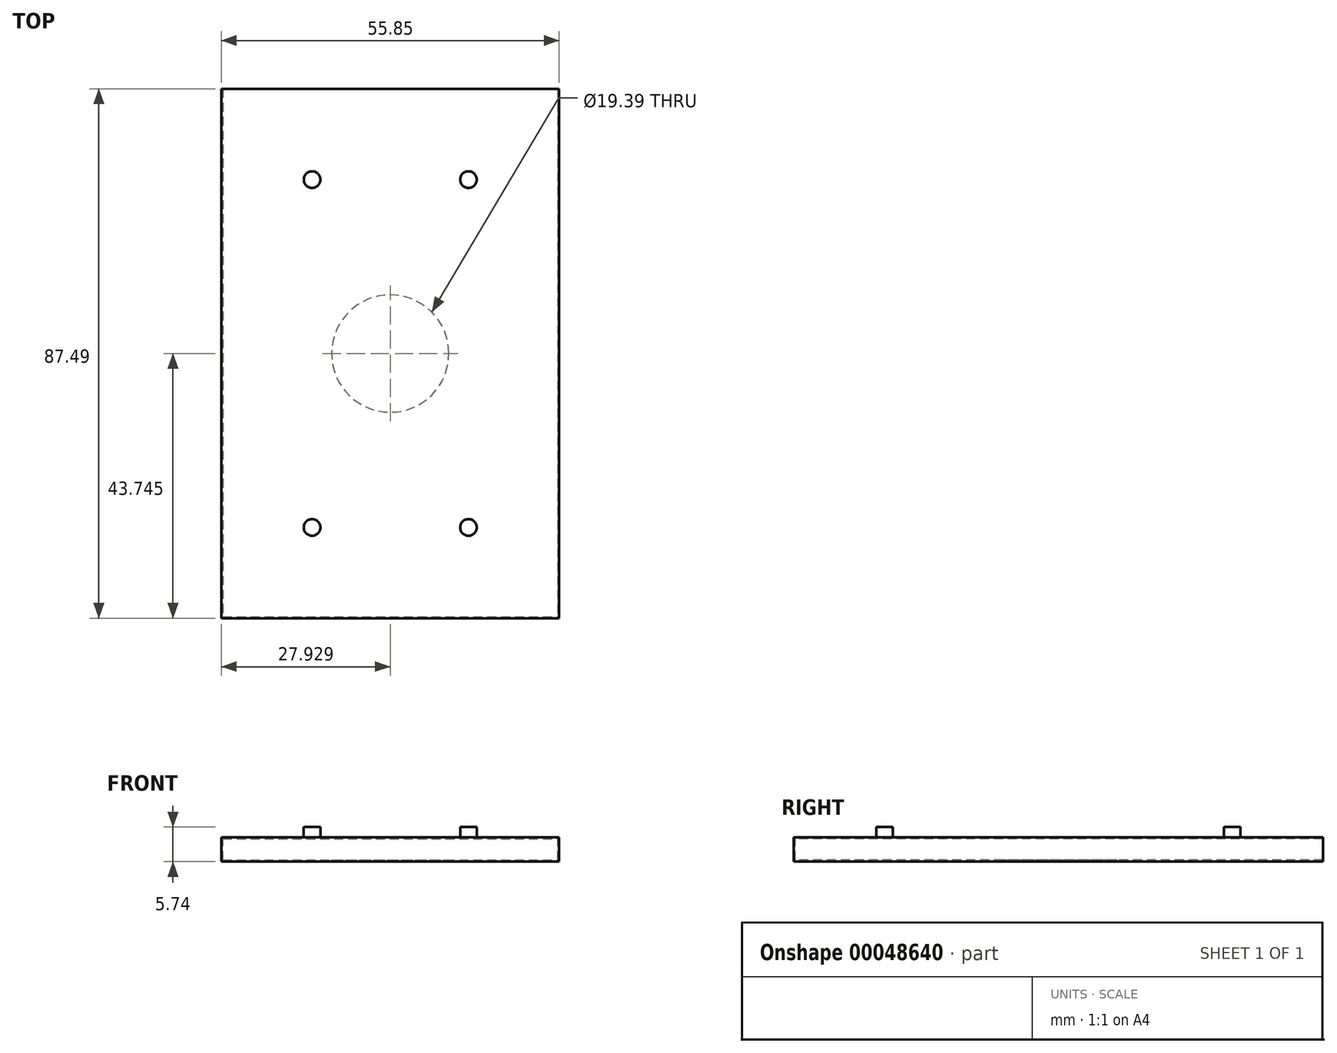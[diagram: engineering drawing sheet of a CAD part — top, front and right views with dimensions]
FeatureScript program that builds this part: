
annotation { "Feature Type Name" : "Feature", "Feature Type Description" : "" }
export const myFeature = defineFeature(function(context is Context, id is Id, definition is map)
    precondition{}
    {
        {
            var Q0;
            Q0=qCreatedBy(makeId("Front.planeOp"),FACE);
            var sketch = newSketch(context, id + "F0", { "sketchPlane" : qUnion([Q0])});
            skLineSegment(sketch, "E0.bottom", {"start": v(-66.96, -20.03) * mm, "end": v(-11.1, -20.03) * mm});
            skLineSegment(sketch, "E0.top", {"start": v(-66.96, -23.03) * mm, "end": v(-11.1, -23.03) * mm});
            skLineSegment(sketch, "E0.left", {"start": v(-66.96, -20.03) * mm, "end": v(-66.96, -23.03) * mm});
            skLineSegment(sketch, "E0.right", {"start": v(-11.1, -20.03) * mm, "end": v(-11.1, -23.03) * mm});
            skSolve(sketch);
        }
        {
            var Q0;
            Q0=makeQuery(id+"F0.imprint","IMPRINT",FACE,{"disambiguationData":[TD([[makeQuery(id+"F0.imprint","IMPRINT",EDGE,{"derivedFrom":sQuery(id+"F0.wireOp",EDGE,"E0.bottom")}),-1.0]])]});
            extrude(context, id + "F1", {"entities" : qUnion([Q0]), "oppositeDirection" : true, "depth" : 87.49 * mm});
        }
        {
            var Q0;
            Q0=makeQuery(id+"F1.opExtrude","SWEPT_FACE",FACE,{"disambiguationData":[OSD([sQuery(id+"F0.wireOp",EDGE,"E0.bottom")])]});
            shell(context, id + "F2", {"entities" : qUnion([Q0]), "thickness" : 0.75 * mm});
        }
        {
            var Q0;
            {var subQ0=sQuery(id+"F0.wireOp",EDGE,"E0.bottom");var subQ1=sQuery(id+"F0.wireOp",EDGE,"E0.top");var subQ2=sQuery(id+"F0.wireOp",EDGE,"E0.left");var subQ3=sQuery(id+"F0.wireOp",EDGE,"E0.right");Q0=makeQuery(id+"F2.opShell","OFFSET_FACE",FACE,{"disambiguationData":[OSD([subQ0,subQ1,subQ2,subQ3]),TDD([makeQuery(id+"F1.opExtrude","CAP_FACE",FACE,{"disambiguationData":[OSD([subQ0,subQ1,subQ2,subQ3])],"isStart":false})])]});}
            extrude(context, id + "F3", {"entities" : qUnion([Q0]), "operationType" : NewBodyOperationType.REMOVE, "oppositeDirection" : true, "depth" : 0.75 * mm});
        }
        {
            var Q0;
            {var subQ0=sQuery(id+"F0.wireOp",EDGE,"E0.top");Q0=makeQuery(id+"F3.boolean.opBoolean","MERGE",FACE,{"derivedFrom":[makeQuery(id+"F2.opShell","OFFSET_FACE",FACE,{"disambiguationData":[OSD([subQ0])]}),makeQuery(id+"F3.opExtrude","SWEPT_FACE",FACE,{"disambiguationData":[OSD([subQ0])]})]});}
            var sketch = newSketch(context, id + "F4", { "sketchPlane" : qUnion([Q0])});
            skPoint(sketch, "E1", {"position": v(-39.03, 87.49) * mm});
            skPoint(sketch, "E2", {"position": v(-49.03, 87.49) * mm});
            skPoint(sketch, "E3", {"position": v(-29.03, 87.49) * mm});
            skLineSegment(sketch, "E4", {"start": v(-49.03, 87.49) * mm, "end": v(-49.03, 94.5) * mm});
            skLineSegment(sketch, "E5", {"start": v(-49.03, 94.5) * mm, "end": v(-29.03, 94.5) * mm});
            skLineSegment(sketch, "E6", {"start": v(-29.03, 94.5) * mm, "end": v(-29.03, 87.49) * mm});
            skPoint(sketch, "E7.end.orphan", {"position": v(-43.53, 87.49) * mm});
            skPoint(sketch, "E7.start.orphan", {"position": v(-34.53, 87.49) * mm});
            skLineSegment(sketch, "E8.bottom", {"start": v(-47.03, 89.5) * mm, "end": v(-31.03, 89.5) * mm});
            skLineSegment(sketch, "E8.top", {"start": v(-47.03, 92.5) * mm, "end": v(-31.03, 92.5) * mm});
            skLineSegment(sketch, "E8.left", {"start": v(-47.03, 89.5) * mm, "end": v(-47.03, 92.5) * mm});
            skLineSegment(sketch, "E8.right", {"start": v(-31.03, 89.5) * mm, "end": v(-31.03, 92.5) * mm});
            skSolve(sketch);
        }
        {
            var Q0;
            {var subQ2=sQuery(id+"F4.wireOp",EDGE,"E4");Q0=makeQuery(id+"F4.imprint","IMPRINT",FACE,{"disambiguationData":[TD([[makeQuery(id+"F4.imprint","IMPRINT",EDGE,{"derivedFrom":subQ2}),-1.0]])]});}
            var Q1;
            Q1=makeQuery(id+"F1.opExtrude","SWEPT_FACE",FACE,{"disambiguationData":[OSD([sQuery(id+"F0.wireOp",EDGE,"E0.top")])]});
            extrude(context, id + "F5", {"entities" : qUnion([Q0]), "operationType" : NewBodyOperationType.ADD, "endBound" : BoundingType.UP_TO_SURFACE, "oppositeDirection" : true, "endBoundEntityFace" : qUnion([Q1]), "depth" : 25 * mm});
        }
        {
            var Q0;
            {var subQ0=sQuery(id+"F0.wireOp",EDGE,"E0.left");Q0=makeQuery(id+"F3.boolean.opBoolean","MERGE",FACE,{"derivedFrom":[makeQuery(id+"F2.opShell","OFFSET_FACE",FACE,{"disambiguationData":[OSD([subQ0])]}),makeQuery(id+"F3.opExtrude","SWEPT_FACE",FACE,{"disambiguationData":[OSD([subQ0])]})]});}
            var sketch = newSketch(context, id + "F6", { "sketchPlane" : qUnion([Q0])});
            skPoint(sketch, "E9", {"position": v(82.49, -21.03) * mm});
            skPoint(sketch, "E10", {"position": v(27.49, -21.03) * mm});
            skArc(sketch, "E11", {"start": v(83.36, -21.03) * mm, "mid": v(82.49, -20.16) * mm, "end": v(81.61, -21.03) * mm});
            skLineSegment(sketch, "E12", {"start": v(82.49, -21.03) * mm, "end": v(83.36, -21.03) * mm});
            skLineSegment(sketch, "E13", {"start": v(82.49, -21.03) * mm, "end": v(81.61, -21.03) * mm});
            skArc(sketch, "E14", {"start": v(28.36, -21.03) * mm, "mid": v(27.49, -20.16) * mm, "end": v(26.61, -21.03) * mm});
            skLineSegment(sketch, "E15", {"start": v(27.49, -21.03) * mm, "end": v(28.36, -21.03) * mm});
            skLineSegment(sketch, "E16", {"start": v(27.49, -21.03) * mm, "end": v(26.61, -21.03) * mm});
            skSolve(sketch);
        }
        {
            var Q0;
            Q0=makeQuery(id+"F6.imprint","IMPRINT",FACE,{"disambiguationData":[TD([[makeQuery(id+"F6.imprint","IMPRINT",EDGE,{"derivedFrom":sQuery(id+"F6.wireOp",EDGE,"E11")}),1.0]])]});
            var Q1;
            Q1=sQuery(id+"F6.wireOp",EDGE,"E13");
            revolve(context, id + "F7", {"operationType" : NewBodyOperationType.ADD, "entities" : qUnion([Q0]), "axis" : qUnion([Q1]), "revolveType" : RevolveType.ONE_DIRECTION, "oppositeDirection" : true, "angle" : 90 * degree});
        }
        {
            var Q0;
            Q0=makeQuery(id+"F6.imprint","IMPRINT",FACE,{"disambiguationData":[TD([[makeQuery(id+"F6.imprint","IMPRINT",EDGE,{"derivedFrom":sQuery(id+"F6.wireOp",EDGE,"E14")}),1.0]])]});
            var Q1;
            Q1=sQuery(id+"F6.wireOp",EDGE,"E16");
            revolve(context, id + "F8", {"operationType" : NewBodyOperationType.ADD, "entities" : qUnion([Q0]), "axis" : qUnion([Q1]), "revolveType" : RevolveType.ONE_DIRECTION, "oppositeDirection" : true, "angle" : 90 * degree});
        }
        {
            var Q0;
            {var subQ0=sQuery(id+"F0.wireOp",EDGE,"E0.right");Q0=makeQuery(id+"F3.boolean.opBoolean","MERGE",FACE,{"derivedFrom":[makeQuery(id+"F2.opShell","OFFSET_FACE",FACE,{"disambiguationData":[OSD([subQ0])]}),makeQuery(id+"F3.opExtrude","SWEPT_FACE",FACE,{"disambiguationData":[OSD([subQ0])]})]});}
            var sketch = newSketch(context, id + "F9", { "sketchPlane" : qUnion([Q0])});
            skPoint(sketch, "E17", {"position": v(-82.49, -21.03) * mm});
            skPoint(sketch, "E18", {"position": v(-27.49, -21.03) * mm});
            skArc(sketch, "E19", {"start": v(-81.61, -21.03) * mm, "mid": v(-82.49, -20.16) * mm, "end": v(-83.36, -21.03) * mm});
            skArc(sketch, "E20", {"start": v(-26.61, -21.03) * mm, "mid": v(-27.49, -20.16) * mm, "end": v(-28.36, -21.03) * mm});
            skLineSegment(sketch, "E21", {"start": v(-83.36, -21.03) * mm, "end": v(-81.61, -21.03) * mm});
            skLineSegment(sketch, "E22", {"start": v(-28.36, -21.03) * mm, "end": v(-26.61, -21.03) * mm});
            skSolve(sketch);
        }
        {
            var Q0;
            Q0=makeQuery(id+"F9.imprint","IMPRINT",FACE,{"disambiguationData":[TD([[makeQuery(id+"F9.imprint","IMPRINT",EDGE,{"derivedFrom":sQuery(id+"F9.wireOp",EDGE,"E19")}),1.0]])]});
            var Q1;
            Q1=sQuery(id+"F9.wireOp",EDGE,"E21");
            revolve(context, id + "F10", {"operationType" : NewBodyOperationType.ADD, "entities" : qUnion([Q0]), "axis" : qUnion([Q1]), "revolveType" : RevolveType.ONE_DIRECTION, "angle" : 90 * degree});
        }
        {
            var Q0;
            Q0=makeQuery(id+"F9.imprint","IMPRINT",FACE,{"disambiguationData":[TD([[makeQuery(id+"F9.imprint","IMPRINT",EDGE,{"derivedFrom":sQuery(id+"F9.wireOp",EDGE,"E20")}),1.0]])]});
            var Q1;
            Q1=sQuery(id+"F9.wireOp",EDGE,"E22");
            revolve(context, id + "F11", {"operationType" : NewBodyOperationType.ADD, "entities" : qUnion([Q0]), "axis" : qUnion([Q1]), "revolveType" : RevolveType.ONE_DIRECTION, "angle" : 90 * degree});
        }
        {
            var Q0;
            {var subQ0=sQuery(id+"F0.wireOp",EDGE,"E0.left");Q0=makeQuery(id+"F2.opShell","OFFSET_EDGE",EDGE,{"disambiguationData":[OSD([subQ0]),TDD([makeQuery(id+"F1.opExtrude","CAP_EDGE",EDGE,{"disambiguationData":[OSD([subQ0])],"isStart":true})])]});}
            fillet(context, id + "F12", {"entities" : qUnion([Q0]), "radius" : 1.5 * mm, "tangentPropagation" : true, "allowEdgeOverflow" : false});
        }
        {
            var Q0;
            {var subQ0=sQuery(id+"F0.wireOp",EDGE,"E0.right");Q0=makeQuery(id+"F2.opShell","OFFSET_EDGE",EDGE,{"disambiguationData":[OSD([subQ0]),TDD([makeQuery(id+"F1.opExtrude","CAP_EDGE",EDGE,{"disambiguationData":[OSD([subQ0])],"isStart":true})])]});}
            fillet(context, id + "F13", {"entities" : qUnion([Q0]), "radius" : 1.5 * mm, "tangentPropagation" : true, "allowEdgeOverflow" : false});
        }
        {
            var Q0;
            {var subQ0=sQuery(id+"F0.wireOp",EDGE,"E0.bottom");var subQ1=sQuery(id+"F0.wireOp",EDGE,"E0.top");var subQ2=sQuery(id+"F0.wireOp",EDGE,"E0.left");var subQ3=sQuery(id+"F0.wireOp",EDGE,"E0.right");Q0=makeQuery(id+"F2.opShell","OFFSET_FACE",FACE,{"disambiguationData":[OSD([subQ0,subQ1,subQ2,subQ3]),TDD([makeQuery(id+"F1.opExtrude","CAP_FACE",FACE,{"disambiguationData":[OSD([subQ0,subQ1,subQ2,subQ3])],"isStart":true})])]});}
            var sketch = newSketch(context, id + "F14", { "sketchPlane" : qUnion([Q0])});
            skPoint(sketch, "E23", {"position": v(39.03, -21.03) * mm});
            skArc(sketch, "E24", {"start": v(39.9, -21.03) * mm, "mid": v(39.03, -20.16) * mm, "end": v(38.16, -21.03) * mm});
            skLineSegment(sketch, "E25", {"start": v(39.9, -21.03) * mm, "end": v(38.16, -21.03) * mm});
            skSolve(sketch);
        }
        {
            var Q0;
            Q0=makeQuery(id+"F14.imprint","IMPRINT",FACE,{"disambiguationData":[TD([[makeQuery(id+"F14.imprint","IMPRINT",EDGE,{"derivedFrom":sQuery(id+"F14.wireOp",EDGE,"E24")}),1.0]])]});
            var Q1;
            Q1=sQuery(id+"F14.wireOp",EDGE,"E25");
            revolve(context, id + "F15", {"operationType" : NewBodyOperationType.ADD, "entities" : qUnion([Q0]), "axis" : qUnion([Q1]), "revolveType" : RevolveType.ONE_DIRECTION, "oppositeDirection" : true, "angle" : 90 * degree});
        }
        {
            var Q0;
            {var subQ0=sQuery(id+"F0.wireOp",EDGE,"E0.top");Q0=makeQuery(id+"F5.boolean.opBoolean","MERGE",FACE,{"derivedFrom":[makeQuery(id+"F1.opExtrude","SWEPT_FACE",FACE,{"disambiguationData":[OSD([subQ0])]}),makeQuery(id+"F5.opExtrude","CAP_FACE",FACE,{"disambiguationData":[OSD([subQ0,sQuery(id+"F4.wireOp",EDGE,"E7"),sQuery(id+"F4.wireOp",EDGE,"01b512f3-2655-4e09-a8f6-d3b41de1633d")])],"isStart":false})]});}
            extrude(context, id + "F16", {"entities" : qUnion([Q0]), "operationType" : NewBodyOperationType.ADD, "depth" : 1 * mm});
        }
        {
            var Q0;
            {var subQ0=sQuery(id+"F4.wireOp",EDGE,"E8.bottom");var subQ1=sQuery(id+"F4.wireOp",EDGE,"E8.left");Q0=makeQuery(id+"F16.boolean.opBoolean","MERGE",EDGE,{"derivedFrom":[makeQuery(id+"F5.opExtrude","SWEPT_EDGE",EDGE,{"disambiguationData":[OSD([subQ0,subQ1])]}),makeQuery(id+"F16.opExtrude","SWEPT_EDGE",EDGE,{"disambiguationData":[OSD([subQ0,subQ1])]})]});}
            fillet(context, id + "F17", {"entities" : qUnion([Q0]), "radius" : 1.5 * mm, "tangentPropagation" : true, "allowEdgeOverflow" : false});
        }
        {
            var Q0;
            {var subQ0=sQuery(id+"F4.wireOp",EDGE,"E8.bottom");var subQ1=sQuery(id+"F4.wireOp",EDGE,"E8.right");Q0=makeQuery(id+"F16.boolean.opBoolean","MERGE",EDGE,{"derivedFrom":[makeQuery(id+"F5.opExtrude","SWEPT_EDGE",EDGE,{"disambiguationData":[OSD([subQ0,subQ1])]}),makeQuery(id+"F16.opExtrude","SWEPT_EDGE",EDGE,{"disambiguationData":[OSD([subQ0,subQ1])]})]});}
            fillet(context, id + "F18", {"entities" : qUnion([Q0]), "radius" : 1.5 * mm, "tangentPropagation" : true, "allowEdgeOverflow" : false});
        }
        {
            var Q0;
            {var subQ0=sQuery(id+"F4.wireOp",EDGE,"E8.top");var subQ1=sQuery(id+"F4.wireOp",EDGE,"E8.right");Q0=makeQuery(id+"F16.boolean.opBoolean","MERGE",EDGE,{"derivedFrom":[makeQuery(id+"F5.opExtrude","SWEPT_EDGE",EDGE,{"disambiguationData":[OSD([subQ0,subQ1])]}),makeQuery(id+"F16.opExtrude","SWEPT_EDGE",EDGE,{"disambiguationData":[OSD([subQ0,subQ1])]})]});}
            fillet(context, id + "F19", {"entities" : qUnion([Q0]), "radius" : 1.5 * mm, "tangentPropagation" : true, "allowEdgeOverflow" : false});
        }
        {
            var Q0;
            {var subQ0=sQuery(id+"F4.wireOp",EDGE,"E8.top");var subQ1=sQuery(id+"F4.wireOp",EDGE,"E8.left");Q0=makeQuery(id+"F16.boolean.opBoolean","MERGE",EDGE,{"derivedFrom":[makeQuery(id+"F5.opExtrude","SWEPT_EDGE",EDGE,{"disambiguationData":[OSD([subQ0,subQ1])]}),makeQuery(id+"F16.opExtrude","SWEPT_EDGE",EDGE,{"disambiguationData":[OSD([subQ0,subQ1])]})]});}
            fillet(context, id + "F20", {"entities" : qUnion([Q0]), "radius" : 1.5 * mm, "tangentPropagation" : true, "allowEdgeOverflow" : false});
        }
        {
            var Q0;
            {var subQ0=sQuery(id+"F4.wireOp",EDGE,"E5");var subQ1=sQuery(id+"F4.wireOp",EDGE,"E6");Q0=makeQuery(id+"F16.boolean.opBoolean","MERGE",EDGE,{"derivedFrom":[makeQuery(id+"F5.opExtrude","SWEPT_EDGE",EDGE,{"disambiguationData":[OSD([subQ0,subQ1])]}),makeQuery(id+"F16.opExtrude","SWEPT_EDGE",EDGE,{"disambiguationData":[OSD([subQ0,subQ1])]})]});}
            fillet(context, id + "F21", {"entities" : qUnion([Q0]), "radius" : 4 * mm, "tangentPropagation" : true, "allowEdgeOverflow" : false});
        }
        {
            var Q0;
            {var subQ0=sQuery(id+"F4.wireOp",EDGE,"E4");var subQ1=sQuery(id+"F4.wireOp",EDGE,"E5");Q0=makeQuery(id+"F16.boolean.opBoolean","MERGE",EDGE,{"derivedFrom":[makeQuery(id+"F5.opExtrude","SWEPT_EDGE",EDGE,{"disambiguationData":[OSD([subQ0,subQ1])]}),makeQuery(id+"F16.opExtrude","SWEPT_EDGE",EDGE,{"disambiguationData":[OSD([subQ0,subQ1])]})]});}
            fillet(context, id + "F22", {"entities" : qUnion([Q0]), "radius" : 4 * mm, "tangentPropagation" : true, "allowEdgeOverflow" : false});
        }
        {
            var Q0;
            Q0=makeQuery(id+"F16.opExtrude","CAP_FACE",FACE,{"disambiguationData":[OSD([sQuery(id+"F0.wireOp",EDGE,"E0.top"),sQuery(id+"F4.wireOp",EDGE,"E4"),sQuery(id+"F4.wireOp",EDGE,"E5"),sQuery(id+"F4.wireOp",EDGE,"E6"),sQuery(id+"F4.wireOp",EDGE,"E8.bottom"),sQuery(id+"F4.wireOp",EDGE,"E8.top"),sQuery(id+"F4.wireOp",EDGE,"E8.left"),sQuery(id+"F4.wireOp",EDGE,"E8.right")])],"isStart":false});
            var sketch = newSketch(context, id + "F23", { "sketchPlane" : qUnion([Q0])});
            skLineSegment(sketch, "E26.bottom", {"start": v(-66.96, -87.49) * mm, "end": v(-11.1, -87.49) * mm});
            skLineSegment(sketch, "E26.top", {"start": v(-66.96, 0) * mm, "end": v(-11.1, 0) * mm});
            skLineSegment(sketch, "E26.left", {"start": v(-66.96, -87.49) * mm, "end": v(-66.96, 0) * mm});
            skLineSegment(sketch, "E26.right", {"start": v(-11.1, -87.49) * mm, "end": v(-11.1, 0) * mm});
            skSolve(sketch);
        }
        {
            var Q0;
            Q0=qSketchRegion(id+"F23",true);
            extrude(context, id + "F24", {"entities" : qUnion([Q0]), "depth" : 4 * mm});
        }
        {
            var Q0;
            Q0=makeQuery(id+"F24.opExtrude","SWEPT_FACE",FACE,{"disambiguationData":[OSD([sQuery(id+"F23.wireOp",EDGE,"E26.bottom")])]});
            shell(context, id + "F25", {"entities" : qUnion([Q0]), "thickness" : 0.25 * mm});
        }
        {
            var Q0;
            Q0=makeQuery(id+"F24.opExtrude","CAP_FACE",FACE,{"disambiguationData":[OSD([sQuery(id+"F23.wireOp",EDGE,"E26.bottom"),sQuery(id+"F23.wireOp",EDGE,"E26.top"),sQuery(id+"F23.wireOp",EDGE,"E26.left"),sQuery(id+"F23.wireOp",EDGE,"E26.right")])],"isStart":false});
            var sketch = newSketch(context, id + "F26", { "sketchPlane" : qUnion([Q0])});
            skPoint(sketch, "E27", {"position": v(-39.03, 0) * mm});
            skPoint(sketch, "E28", {"position": v(-11.1, -43.74) * mm});
            skPoint(sketch, "E29", {"position": v(-39.03, -43.74) * mm});
            skCircle(sketch, "E30", {"center": v(-39.03, -43.74) * mm, "radius": 9.7 * mm});
            skSolve(sketch);
        }
        {
            var Q0;
            Q0=qSketchRegion(id+"F26",true);
            extrude(context, id + "F27", {"entities" : qUnion([Q0]), "operationType" : NewBodyOperationType.REMOVE, "endBound" : BoundingType.UP_TO_NEXT, "oppositeDirection" : true, "depth" : 25 * mm});
        }
        {
            var Q0;
            Q0=makeQuery(id+"F1.opExtrude","SWEPT_BODY",BODY,{"disambiguationData":[OSD([sQuery(id+"F0.wireOp",EDGE,"E0.bottom"),sQuery(id+"F0.wireOp",EDGE,"E0.top"),sQuery(id+"F0.wireOp",EDGE,"E0.left"),sQuery(id+"F0.wireOp",EDGE,"E0.right")])]});
            deleteBodies(context, id + "F28", {"entities" : qUnion([Q0])});
        }
        {
            var Q0;
            Q0=makeQuery(id+"F24.opExtrude","CAP_FACE",FACE,{"disambiguationData":[OSD([sQuery(id+"F23.wireOp",EDGE,"E26.bottom"),sQuery(id+"F23.wireOp",EDGE,"E26.top"),sQuery(id+"F23.wireOp",EDGE,"E26.left"),sQuery(id+"F23.wireOp",EDGE,"E26.right")])],"isStart":true});
            var sketch = newSketch(context, id + "F29", { "sketchPlane" : qUnion([Q0])});
            skPoint(sketch, "E31", {"position": v(-26.1, 15) * mm});
            skPoint(sketch, "E32", {"position": v(-51.96, 15) * mm});
            skPoint(sketch, "E33", {"position": v(-51.96, 72.49) * mm});
            skPoint(sketch, "E34", {"position": v(-26.1, 72.49) * mm});
            skCircle(sketch, "E35", {"center": v(-51.96, 15) * mm, "radius": 1.38 * mm});
            skCircle(sketch, "E36", {"center": v(-26.1, 15) * mm, "radius": 1.38 * mm});
            skCircle(sketch, "E37", {"center": v(-26.1, 72.49) * mm, "radius": 1.38 * mm});
            skCircle(sketch, "E38", {"center": v(-51.96, 72.49) * mm, "radius": 1.38 * mm});
            skSolve(sketch);
        }
        {
            var Q0;
            Q0=makeQuery(id+"F29.imprint","IMPRINT",FACE,{"disambiguationData":[TD([[makeQuery(id+"F29.imprint","IMPRINT",EDGE,{"derivedFrom":sQuery(id+"F29.wireOp",EDGE,"E35")}),1.0]])]});
            var Q1;
            Q1=makeQuery(id+"F29.imprint","IMPRINT",FACE,{"disambiguationData":[TD([[makeQuery(id+"F29.imprint","IMPRINT",EDGE,{"derivedFrom":sQuery(id+"F29.wireOp",EDGE,"E36")}),1.0]])]});
            var Q2;
            Q2=makeQuery(id+"F29.imprint","IMPRINT",FACE,{"disambiguationData":[TD([[makeQuery(id+"F29.imprint","IMPRINT",EDGE,{"derivedFrom":sQuery(id+"F29.wireOp",EDGE,"E37")}),1.0]])]});
            var Q3;
            Q3=makeQuery(id+"F29.imprint","IMPRINT",FACE,{"disambiguationData":[TD([[makeQuery(id+"F29.imprint","IMPRINT",EDGE,{"derivedFrom":sQuery(id+"F29.wireOp",EDGE,"E38")}),1.0]])]});
            extrude(context, id + "F30", {"entities" : qUnion([Q0, Q1, Q2, Q3]), "operationType" : NewBodyOperationType.ADD, "depth" : 1.74 * mm});
        }
    });
